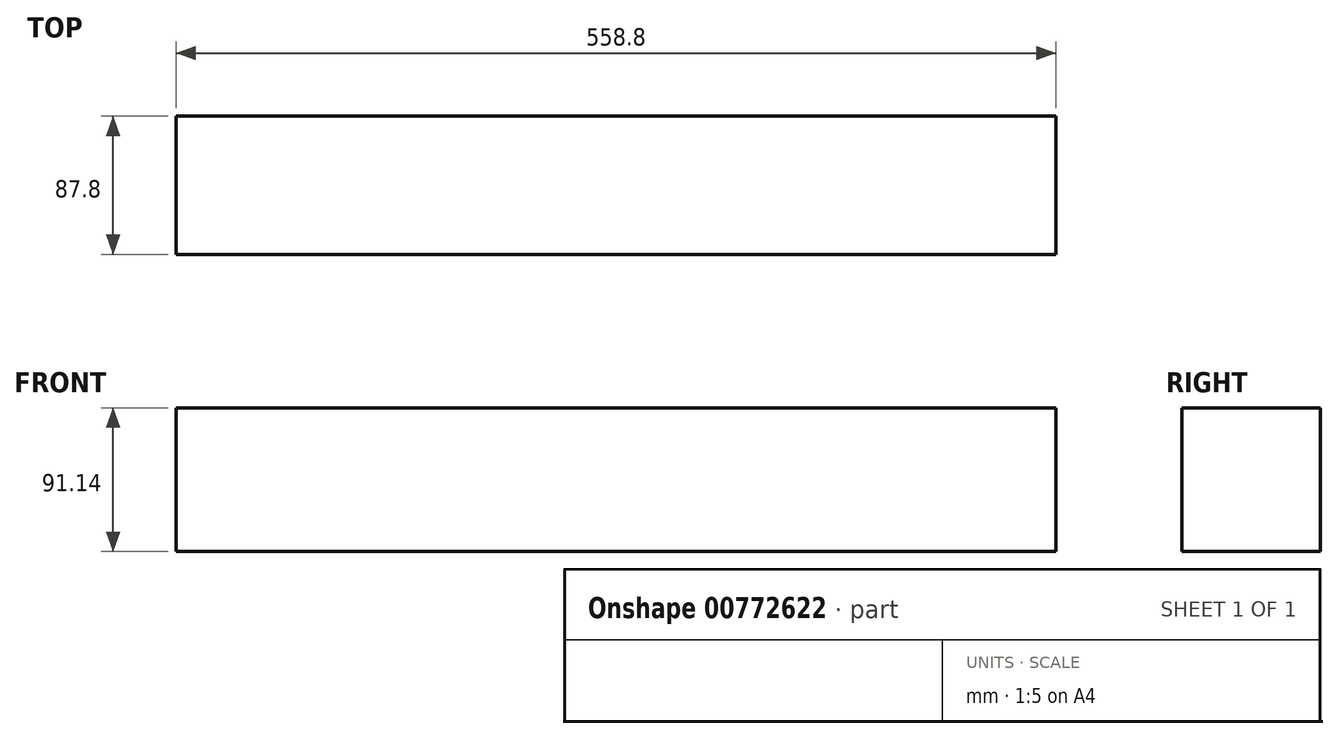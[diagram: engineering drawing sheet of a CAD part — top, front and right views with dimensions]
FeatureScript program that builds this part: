
annotation { "Feature Type Name" : "Feature", "Feature Type Description" : "" }
export const myFeature = defineFeature(function(context is Context, id is Id, definition is map)
    precondition{}
    {
        {
            var Q0;
            Q0=qCreatedBy(makeId("Right.planeOp"),FACE);
            var sketch = newSketch(context, id + "F0", { "sketchPlane" : qUnion([Q0])});
            skLineSegment(sketch, "E0.bottom", {"start": v(43.9, -45.57) * mm, "end": v(-43.9, -45.57) * mm});
            skLineSegment(sketch, "E0.top", {"start": v(43.9, 45.57) * mm, "end": v(-43.9, 45.57) * mm});
            skLineSegment(sketch, "E0.left", {"start": v(43.9, -45.57) * mm, "end": v(43.9, 45.57) * mm});
            skLineSegment(sketch, "E0.right", {"start": v(-43.9, -45.57) * mm, "end": v(-43.9, 45.57) * mm});
            skPoint(sketch, "E0.middle", {"position": v(0, 0) * mm});
            skSolve(sketch);
        }
        {
            var Q0;
            Q0=makeQuery(id+"F0.imprint","IMPRINT",FACE,{"disambiguationData":[TD([[makeQuery(id+"F0.imprint","IMPRINT",EDGE,{"derivedFrom":sQuery(id+"F0.wireOp",EDGE,"E0.bottom")}),-1.0]])]});
            extrude(context, id + "F1", {"entities" : qUnion([Q0]), "depth" : 558.8 * mm, "offsetDistance" : 25.4 * mm});
        }
    });
